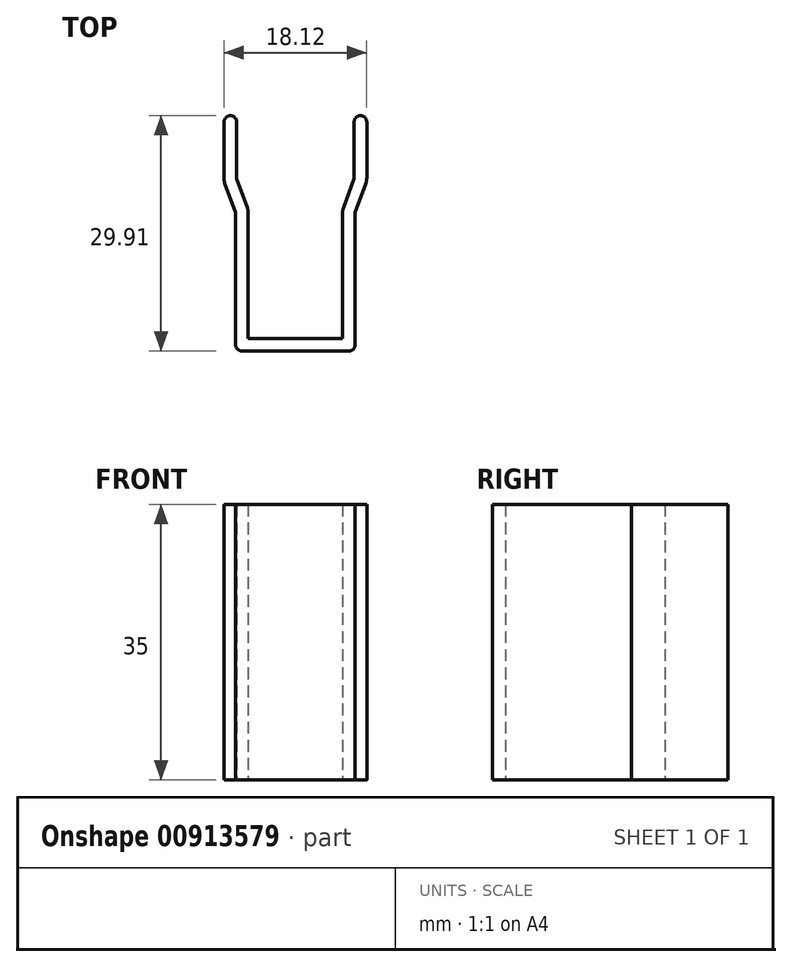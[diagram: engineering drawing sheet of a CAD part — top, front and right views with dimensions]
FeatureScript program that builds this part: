
annotation { "Feature Type Name" : "Feature", "Feature Type Description" : "" }
export const myFeature = defineFeature(function(context is Context, id is Id, definition is map)
    precondition{}
    {
        {
            var Q0;
            Q0=qCreatedBy(makeId("Top.planeOp"),FACE);
            var sketch = newSketch(context, id + "F0", { "sketchPlane" : qUnion([Q0])});
            skLineSegment(sketch, "E0.bottom", {"start": v(0, 0) * mm, "end": v(-12, 0) * mm});
            skLineSegment(sketch, "E0.left", {"start": v(0, 0) * mm, "end": v(0, 16) * mm});
            skLineSegment(sketch, "E0.right", {"start": v(-12, 0) * mm, "end": v(-12, 16) * mm});
            skLineSegment(sketch, "E1.bottom", {"start": v(1.6, -1.6) * mm, "end": v(-13.6, -1.6) * mm});
            skLineSegment(sketch, "E1.left", {"start": v(1.6, -1.6) * mm, "end": v(1.6, 16) * mm});
            skLineSegment(sketch, "E1.right", {"start": v(-13.6, -1.6) * mm, "end": v(-13.6, 16) * mm});
            skLineSegment(sketch, "E2", {"start": v(-12, 16) * mm, "end": v(-13.6, 16) * mm});
            skLineSegment(sketch, "E3", {"start": v(-13.6, 16) * mm, "end": v(-12, 16) * mm});
            skLineSegment(sketch, "E4", {"start": v(0, 16) * mm, "end": v(1.6, 16) * mm});
            skLineSegment(sketch, "E5.bottom", {"start": v(-13.6, 16) * mm, "end": v(-12.1, 16.55) * mm});
            skLineSegment(sketch, "E5.top", {"start": v(-14.97, 19.76) * mm, "end": v(-13.46, 20.3) * mm});
            skLineSegment(sketch, "E5.left", {"start": v(-13.6, 16) * mm, "end": v(-14.97, 19.76) * mm});
            skLineSegment(sketch, "E5.right", {"start": v(-12.1, 16.55) * mm, "end": v(-13.46, 20.3) * mm});
            skLineSegment(sketch, "E6", {"start": v(-6, -4.52) * mm, "end": v(-6, 27.97) * mm, "construction": true});
            skPoint(sketch, "E6.startSnap0", {"position": v(-6, -1.6) * mm});
            skLineSegment(sketch, "E7.bottom", {"start": v(-15.06, 20.3) * mm, "end": v(-13.46, 20.3) * mm});
            skLineSegment(sketch, "E7.top", {"start": v(-15.06, 28.3) * mm, "end": v(-13.46, 28.3) * mm});
            skLineSegment(sketch, "E7.left", {"start": v(-15.06, 20.3) * mm, "end": v(-15.06, 28.3) * mm});
            skLineSegment(sketch, "E7.right", {"start": v(-13.46, 20.3) * mm, "end": v(-13.46, 28.3) * mm});
            skArc(sketch, "E8", {"start": v(-12, 16) * mm, "mid": v(-12.02, 16.28) * mm, "end": v(-12.1, 16.55) * mm});
            skArc(sketch, "E9", {"start": v(-15.06, 20.3) * mm, "mid": v(-15.04, 20.03) * mm, "end": v(-14.97, 19.76) * mm});
            skArc(sketch, "E10.MirrorCS", {"start": v(0, 16) * mm, "mid": v(0.02, 16.28) * mm, "end": v(0.1, 16.55) * mm});
            skArc(sketch, "E11.MirrorCS", {"start": v(3.06, 20.3) * mm, "mid": v(3.04, 20.03) * mm, "end": v(2.97, 19.76) * mm});
            skLineSegment(sketch, "E12.MirrorCS", {"start": v(3.06, 20.3) * mm, "end": v(1.46, 20.3) * mm});
            skLineSegment(sketch, "E13.MirrorCS", {"start": v(2.97, 19.76) * mm, "end": v(1.46, 20.3) * mm});
            skLineSegment(sketch, "E14.MirrorCS", {"start": v(3.06, 28.3) * mm, "end": v(1.46, 28.3) * mm});
            skLineSegment(sketch, "E15.MirrorCS", {"start": v(3.06, 20.3) * mm, "end": v(3.06, 28.3) * mm});
            skLineSegment(sketch, "E16.MirrorCS", {"start": v(1.6, 16) * mm, "end": v(0.1, 16.55) * mm});
            skLineSegment(sketch, "E17.MirrorCS", {"start": v(1.46, 20.3) * mm, "end": v(1.46, 28.3) * mm});
            skLineSegment(sketch, "E18.MirrorCS", {"start": v(1.6, 16) * mm, "end": v(0, 16) * mm});
            skLineSegment(sketch, "E19.MirrorCS", {"start": v(1.6, 16) * mm, "end": v(2.97, 19.76) * mm});
            skLineSegment(sketch, "E20.MirrorCS", {"start": v(0.1, 16.55) * mm, "end": v(1.46, 20.3) * mm});
            skSolve(sketch);
        }
        {
            var Q0;
            Q0 = qSketchRegion(id + "F0", true);
            extrude(context, id + "F1", {"entities" : qUnion([Q0]), "depth" : 35 * mm, "offsetDistance" : 25 * mm});
        }
        {
            var Q0;
            Q0=makeQuery(id+"F1.opExtrude","SWEPT_EDGE",EDGE,{"disambiguationData":[OSD([sQuery(id+"F0.wireOp",EDGE,"E1.bottom"),sQuery(id+"F0.wireOp",EDGE,"E1.left")])]});
            var Q1;
            Q1=makeQuery(id+"F1.opExtrude","SWEPT_EDGE",EDGE,{"disambiguationData":[OSD([sQuery(id+"F0.wireOp",EDGE,"E1.bottom"),sQuery(id+"F0.wireOp",EDGE,"E1.right")])]});
            var Q2;
            Q2=makeQuery(id+"F1.opExtrude","SWEPT_EDGE",EDGE,{"disambiguationData":[OSD([sQuery(id+"F0.wireOp",EDGE,"E7.top"),sQuery(id+"F0.wireOp",EDGE,"E7.left")])]});
            var Q3;
            Q3=makeQuery(id+"F1.opExtrude","SWEPT_EDGE",EDGE,{"disambiguationData":[OSD([sQuery(id+"F0.wireOp",EDGE,"E14.MirrorCS"),sQuery(id+"F0.wireOp",EDGE,"E15.MirrorCS")])]});
            var Q4;
            Q4=makeQuery(id+"F1.opExtrude","SWEPT_EDGE",EDGE,{"disambiguationData":[OSD([sQuery(id+"F0.wireOp",EDGE,"E14.MirrorCS"),sQuery(id+"F0.wireOp",EDGE,"E17.MirrorCS")])]});
            var Q5;
            Q5=makeQuery(id+"F1.opExtrude","SWEPT_EDGE",EDGE,{"disambiguationData":[OSD([sQuery(id+"F0.wireOp",EDGE,"E7.top"),sQuery(id+"F0.wireOp",EDGE,"E7.right")])]});
            fillet(context, id + "F2", {"entities" : qUnion([Q0, Q1, Q2, Q3, Q4, Q5]), "radius" : .8 * mm, "tangentPropagation" : true, "allowEdgeOverflow" : false});
        }
    });
